# Revit family: Shower_Base-Acorn-TerrazzoWare-SBS-36-3F new
name_source: partatom
category: Plumbing Fixtures
units: mm (PartAtom-declared; Revit-internal decimal feet)

## family parameters
Always vertical = No
Cut with Voids When Loaded = No
OmniClass Number = 23.45.05.14.17
OmniClass Title = Showers
Part Type = Normal
Room Calculation Point = No
Round Connector Dimension = Use Diameter
Shared = Yes
Work Plane-Based = Yes

## types (1)
- SBS-36-3F
    Assembly Code = D2010700
    Body Material = Portland_Cement-Acorn-Terrazzo
    CW Connection = No
    CWFU = 0
    Compressive Strength = 3,000 PSI min.
    Default Elevation = 0"
    Description = 36" x 36" Terrazzo Shower Base, 3-Flange
    Flange Height = 1 1/2"
    HW Connection = No
    HWFU = 0
    Height = 4"
    Installation Type = Floor Mounted
    KDG2 - Rubber Drain Gasket for 2" Waste Pipe = No
    Length = 36"
    Manufacturer = Acorn Engineering
    Model = SBS-36-3F
    Product Documentation Link = https://www.acorneng.com
    Product Page URL = https://www.acorneng.com
    Tiling Flange Material = Stainless Steel-Acorn-Galvanized
    URL = https://www.acorneng.com
    VRS - Vandal Resistant Strainer = No
    Vent Connection = No
    WFU = 4
    Warranty Information = 1 year limited warranty
    Waste Connection = Yes
    Waste Connection Diameter = 2"
    Waste Connection Radius = 1"
    Width = 36"

## geometry (parser evidence)
native form markers: Sweep x3
no freeform markers — native parametric forms only
